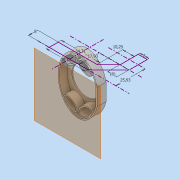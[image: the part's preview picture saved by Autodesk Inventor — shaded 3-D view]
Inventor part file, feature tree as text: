
AUTODESK INVENTOR PART (.ipt)
format: ipt  version: 2019 (Build 230136000, 136)  size: 250,880 bytes
history: native  units: mm
features: other x2, sketch x2, extrude x2, shell x2
ambient origin geometry x8: Origin, YZ Plane, XZ Plane, XY Plane, X Axis, Y Axis, Z Axis, Center Point
bodies: Body1 (feature_tree), Body2 (feature_tree)
feature tree (8):
  other  "Твердое тело1"
  sketch  "Эскиз1"
  extrude  "Выдавливание1"  Depth=34.31mm
  sketch  "Эскиз7"
  shell  "сам корпус"  Thickness=8.0mm
  extrude  "Выдавливание10"  Depth=34.31mm
  shell  "Оболочка9"  Thickness=8.0mm
  other  "Твердое тело6"
